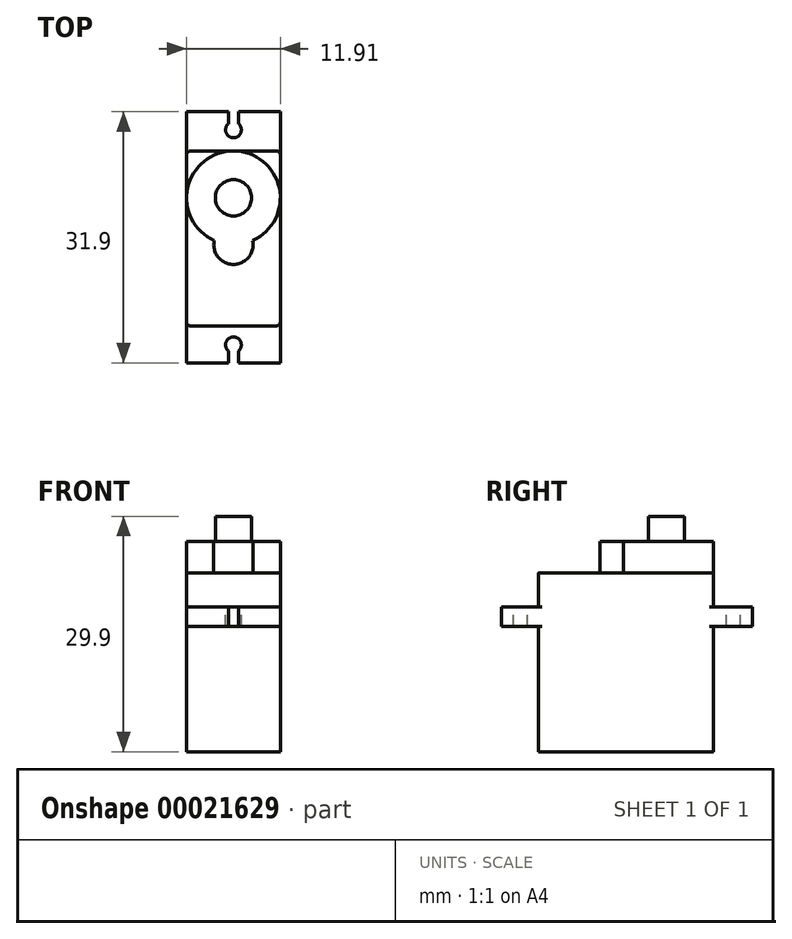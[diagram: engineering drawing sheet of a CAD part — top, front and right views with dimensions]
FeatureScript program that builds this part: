
annotation { "Feature Type Name" : "Feature", "Feature Type Description" : "" }
export const myFeature = defineFeature(function(context is Context, id is Id, definition is map)
    precondition{}
    {
        {
            var Q0;
            Q0=qCreatedBy(makeId("Top.planeOp"),FACE);
            var sketch = newSketch(context, id + "F0", { "sketchPlane" : qUnion([Q0])});
            skLineSegment(sketch, "E0", {"start": v(0, 0.5) * mm, "end": v(0, 21.73) * mm});
            skLineSegment(sketch, "E1", {"start": v(0.5, 22.23) * mm, "end": v(11.4, 22.23) * mm});
            skLineSegment(sketch, "E2", {"start": v(11.9, 21.73) * mm, "end": v(11.9, 0.5) * mm});
            skLineSegment(sketch, "E3", {"start": v(11.4, 0) * mm, "end": v(0.5, 0) * mm});
            skPoint(sketch, "E4.visualSharp", {"position": v(0, 22.23) * mm});
            skArc(sketch, "E4.filletArc", {"start": v(0.5, 22.23) * mm, "mid": v(0.15, 22.08) * mm, "end": v(0, 21.73) * mm});
            skPoint(sketch, "E5.visualSharp", {"position": v(11.9, 22.23) * mm});
            skArc(sketch, "E5.filletArc", {"start": v(11.9, 21.73) * mm, "mid": v(11.76, 22.08) * mm, "end": v(11.4, 22.23) * mm});
            skPoint(sketch, "E6.visualSharp", {"position": v(11.9, 0) * mm});
            skArc(sketch, "E6.filletArc", {"start": v(11.4, 0) * mm, "mid": v(11.76, 0.15) * mm, "end": v(11.9, 0.5) * mm});
            skPoint(sketch, "E7.visualSharp", {"position": v(0, 0) * mm});
            skArc(sketch, "E7.filletArc", {"start": v(0, 0.5) * mm, "mid": v(0.15, 0.15) * mm, "end": v(0.5, 0) * mm});
            skSolve(sketch);
        }
        {
            var Q0;
            Q0=makeQuery(id+"F0.imprint","IMPRINT",FACE,{"disambiguationData":[TD([[makeQuery(id+"F0.imprint","IMPRINT",EDGE,{"derivedFrom":sQuery(id+"F0.wireOp",EDGE,"E0")}),-1.0]])]});
            extrude(context, id + "F1", {"entities" : qUnion([Q0]), "depth" : 16 * mm});
        }
        {
            var Q0;
            Q0=makeQuery(id+"F1.opExtrude","CAP_FACE",FACE,{"disambiguationData":[OSD([sQuery(id+"F0.wireOp",EDGE,"E0"),sQuery(id+"F0.wireOp",EDGE,"E1"),sQuery(id+"F0.wireOp",EDGE,"E2"),sQuery(id+"F0.wireOp",EDGE,"E3"),sQuery(id+"F0.wireOp",EDGE,"E4.filletArc"),sQuery(id+"F0.wireOp",EDGE,"E5.filletArc"),sQuery(id+"F0.wireOp",EDGE,"E6.filletArc"),sQuery(id+"F0.wireOp",EDGE,"E7.filletArc")])],"isStart":false});
            extrude(context, id + "F2", {"entities" : qUnion([Q0]), "operationType" : NewBodyOperationType.ADD, "depth" : 6.7 * mm});
        }
        {
            var Q0;
            Q0=makeQuery(id+"F2.opExtrude","CAP_FACE",FACE,{"disambiguationData":[OSD([sQuery(id+"F0.wireOp",EDGE,"E0"),sQuery(id+"F0.wireOp",EDGE,"E1"),sQuery(id+"F0.wireOp",EDGE,"E2"),sQuery(id+"F0.wireOp",EDGE,"E3"),sQuery(id+"F0.wireOp",EDGE,"E4.filletArc"),sQuery(id+"F0.wireOp",EDGE,"E5.filletArc"),sQuery(id+"F0.wireOp",EDGE,"E6.filletArc"),sQuery(id+"F0.wireOp",EDGE,"E7.filletArc")])],"isStart":false});
            var sketch = newSketch(context, id + "F3", { "sketchPlane" : qUnion([Q0])});
            skLineSegment(sketch, "E8", {"start": v(0, 16.27) * mm, "end": v(11.9, 16.27) * mm, "construction": true});
            skArc(sketch, "E9", {"start": v(8.4, 10.84) * mm, "mid": v(5.95, 22.23) * mm, "end": v(3.5, 10.84) * mm});
            skLineSegment(sketch, "E10", {"start": v(5.95, 16.27) * mm, "end": v(5.95, 5.27) * mm, "construction": true});
            skArc(sketch, "E11", {"start": v(3.5, 10.84) * mm, "mid": v(5.95, 7.82) * mm, "end": v(8.4, 10.84) * mm});
            skSolve(sketch);
        }
        {
            var Q0;
            {var subQ0=sQuery(id+"F3.wireOp",EDGE,"E11");Q0=makeQuery(id+"F3.imprint","IMPRINT",FACE,{"disambiguationData":[TD([[makeQuery(id+"F3.imprint","IMPRINT",EDGE,{"derivedFrom":subQ0}),1.0]])]});}
            extrude(context, id + "F4", {"entities" : qUnion([Q0]), "operationType" : NewBodyOperationType.ADD, "depth" : 4 * mm});
        }
        {
            var Q0;
            Q0=makeQuery(id+"F4.opExtrude","CAP_FACE",FACE,{"disambiguationData":[OSD([sQuery(id+"F3.wireOp",EDGE,"E9"),sQuery(id+"F3.wireOp",EDGE,"E11")])],"isStart":false});
            var sketch = newSketch(context, id + "F5", { "sketchPlane" : qUnion([Q0])});
            skLineSegment(sketch, "E12", {"start": v(5.95, 22.23) * mm, "end": v(5.95, 7.82) * mm, "construction": true});
            skLineSegment(sketch, "E13", {"start": v(0, 16.27) * mm, "end": v(11.9, 16.27) * mm, "construction": true});
            skCircle(sketch, "E14", {"center": v(5.95, 16.27) * mm, "radius": 2.3 * mm});
            skSolve(sketch);
        }
        {
            var Q0;
            Q0=makeQuery(id+"F5.imprint","IMPRINT",FACE,{"disambiguationData":[TD([[makeQuery(id+"F5.imprint","IMPRINT",EDGE,{"derivedFrom":sQuery(id+"F5.wireOp",EDGE,"E14")}),1.0]])]});
            extrude(context, id + "F6", {"entities" : qUnion([Q0]), "operationType" : NewBodyOperationType.ADD, "depth" : 3.2 * mm});
        }
        {
            var Q0;
            {var subQ0=sQuery(id+"F0.wireOp",EDGE,"E3");Q0=makeQuery(id+"F2.boolean.opBoolean","MERGE",FACE,{"derivedFrom":[makeQuery(id+"F1.opExtrude","SWEPT_FACE",FACE,{"disambiguationData":[OSD([subQ0])]}),makeQuery(id+"F2.opExtrude","SWEPT_FACE",FACE,{"disambiguationData":[OSD([subQ0])]})]});}
            var sketch = newSketch(context, id + "F7", { "sketchPlane" : qUnion([Q0])});
            skLineSegment(sketch, "E15", {"start": v(5.95, 22.7) * mm, "end": v(5.95, 0) * mm, "construction": true});
            skLineSegment(sketch, "E16", {"start": v(0.5, 18.4) * mm, "end": v(11.4, 18.4) * mm, "construction": true});
            skLineSegment(sketch, "E17", {"start": v(0, 18.4) * mm, "end": v(11.9, 18.4) * mm});
            skLineSegment(sketch, "E18", {"start": v(11.9, 18.4) * mm, "end": v(11.9, 15.9) * mm});
            skLineSegment(sketch, "E19", {"start": v(11.9, 15.9) * mm, "end": v(0, 15.9) * mm});
            skLineSegment(sketch, "E20", {"start": v(0, 15.9) * mm, "end": v(0, 18.4) * mm});
            skSolve(sketch);
        }
        {
            var Q0;
            {var subQ7=sQuery(id+"F7.wireOp",EDGE,"E18");Q0=makeQuery(id+"F7.imprint","IMPRINT",FACE,{"disambiguationData":[TD([[makeQuery(id+"F7.imprint","IMPRINT",EDGE,{"derivedFrom":subQ7}),-1.0]])]});}
            var Q1;
            {var subQ0=sQuery(id+"F0.wireOp",EDGE,"E3");var subQ1=sQuery(id+"F0.wireOp",EDGE,"E7.filletArc");var subQ2=makeQuery(id+"F2.boolean.opBoolean","MERGE",EDGE,{"derivedFrom":[makeQuery(id+"F1.opExtrude","SWEPT_EDGE",EDGE,{"disambiguationData":[OSD([subQ0,subQ1])]}),makeQuery(id+"F2.opExtrude","SWEPT_EDGE",EDGE,{"disambiguationData":[OSD([subQ0,subQ1])]})]});var subQ5=sQuery(id+"F7.wireOp",EDGE,"E17");var subQ6=makeQuery(id+"F7.imprint","INTERSECT",VERTEX,{"derivedFrom":[subQ2,subQ5]});Q1=makeQuery(id+"F7.imprint","IMPRINT",FACE,{"disambiguationData":[TD([[makeQuery(id+"F7.imprint","IMPRINT",EDGE,{"disambiguationData":[TD([[subQ6,-1.0]])],"derivedFrom":subQ5}),-1.0]])]});}
            var Q2;
            {var subQ7=sQuery(id+"F7.wireOp",EDGE,"E20");Q2=makeQuery(id+"F7.imprint","IMPRINT",FACE,{"disambiguationData":[TD([[makeQuery(id+"F7.imprint","IMPRINT",EDGE,{"derivedFrom":subQ7}),-1.0]])]});}
            extrude(context, id + "F8", {"entities" : qUnion([Q0, Q1, Q2]), "operationType" : NewBodyOperationType.ADD, "oppositeDirection" : true, "depth" : 1 * mm});
        }
        {
            var Q0;
            {var subQ0=sQuery(id+"F0.wireOp",EDGE,"E3");Q0=makeQuery(id+"F8.boolean.opBoolean","MERGE",FACE,{"derivedFrom":[makeQuery(id+"F2.boolean.opBoolean","MERGE",FACE,{"derivedFrom":[makeQuery(id+"F1.opExtrude","SWEPT_FACE",FACE,{"disambiguationData":[OSD([subQ0])]}),makeQuery(id+"F2.opExtrude","SWEPT_FACE",FACE,{"disambiguationData":[OSD([subQ0])]})]}),makeQuery(id+"F8.opExtrude","CAP_FACE",FACE,{"disambiguationData":[OSD([sQuery(id+"F7.wireOp",EDGE,"E17"),sQuery(id+"F7.wireOp",EDGE,"E18"),sQuery(id+"F7.wireOp",EDGE,"E19"),sQuery(id+"F7.wireOp",EDGE,"E20")])],"isStart":true})]});}
            var sketch = newSketch(context, id + "F9", { "sketchPlane" : qUnion([Q0])});
            skLineSegment(sketch, "E21", {"start": v(0.5, 18.4) * mm, "end": v(11.4, 18.4) * mm});
            skLineSegment(sketch, "E22", {"start": v(0.5, 15.9) * mm, "end": v(11.4, 15.9) * mm});
            skSolve(sketch);
        }
        {
            var Q0;
            Q0=makeQuery(id+"F9.imprint","IMPRINT",FACE,{"disambiguationData":[TD([[makeQuery(id+"F9.imprint","IMPRINT",EDGE,{"derivedFrom":sQuery(id+"F9.wireOp",EDGE,"E21")}),-1.0]])]});
            extrude(context, id + "F10", {"entities" : qUnion([Q0]), "operationType" : NewBodyOperationType.ADD, "depth" : 4.7 * mm});
        }
        {
            var Q0;
            Q0=makeQuery(id+"F10.opExtrude","CAP_FACE",FACE,{"disambiguationData":[OSD([sQuery(id+"F7.wireOp",EDGE,"E17"),sQuery(id+"F7.wireOp",EDGE,"E18"),sQuery(id+"F7.wireOp",EDGE,"E19"),sQuery(id+"F7.wireOp",EDGE,"E20"),sQuery(id+"F9.wireOp",EDGE,"E21"),sQuery(id+"F9.wireOp",EDGE,"E22")])],"isStart":false});
            extrude(context, id + "F11", {"entities" : qUnion([Q0]), "operationType" : NewBodyOperationType.ADD, "oppositeDirection" : true, "depth" : 31.9 * mm});
        }
        {
            var Q0;
            {var subQ0=sQuery(id+"F7.wireOp",EDGE,"E17");var subQ1=makeQuery(id+"F8.opExtrude","SWEPT_FACE",FACE,{"disambiguationData":[OSD([subQ0])]});var subQ8=sQuery(id+"F0.wireOp",EDGE,"E0");var subQ10=sQuery(id+"F0.wireOp",EDGE,"E2");Q0=makeQuery(id+"F10.boolean.opBoolean","MERGE",FACE,{"derivedFrom":[makeQuery(id+"F8.boolean.opBoolean","SPLIT",FACE,{"disambiguationData":[TD([makeQuery(id+"F1.opExtrude","SWEPT_FACE",FACE,{"disambiguationData":[OSD([subQ8])]})])],"derivedFrom":subQ1}),makeQuery(id+"F8.boolean.opBoolean","SPLIT",FACE,{"disambiguationData":[TD([makeQuery(id+"F1.opExtrude","SWEPT_FACE",FACE,{"disambiguationData":[OSD([subQ10])]})])],"derivedFrom":subQ1}),makeQuery(id+"F10.opExtrude","SWEPT_FACE",FACE,{"disambiguationData":[OSD([subQ0,sQuery(id+"F9.wireOp",EDGE,"E21")])]})]});}
            var sketch = newSketch(context, id + "F12", { "sketchPlane" : qUnion([Q0])});
            skLineSegment(sketch, "E23", {"start": v(0, -2.4) * mm, "end": v(11.9, -2.4) * mm, "construction": true});
            skArc(sketch, "E24", {"start": v(6.6, -3.16) * mm, "mid": v(5.95, -1.4) * mm, "end": v(5.3, -3.16) * mm});
            skLineSegment(sketch, "E25", {"start": v(5.95, -2.4) * mm, "end": v(5.95, -4.7) * mm, "construction": true});
            skLineSegment(sketch, "E26", {"start": v(6.6, -4.7) * mm, "end": v(6.6, -3.16) * mm});
            skLineSegment(sketch, "E27", {"start": v(5.3, -4.7) * mm, "end": v(5.3, -3.16) * mm});
            skSolve(sketch);
        }
        {
            var Q0;
            Q0=makeQuery(id+"F12.imprint","IMPRINT",FACE,{"disambiguationData":[TD([[makeQuery(id+"F12.imprint","IMPRINT",EDGE,{"derivedFrom":sQuery(id+"F12.wireOp",EDGE,"E24")}),1.0]])]});
            extrude(context, id + "F13", {"entities" : qUnion([Q0]), "operationType" : NewBodyOperationType.REMOVE, "endBound" : BoundingType.UP_TO_NEXT, "oppositeDirection" : true, "depth" : 25.4 * mm});
        }
        {
            var Q0;
            Q0=makeQuery(id+"F11.opExtrude","SWEPT_FACE",FACE,{"disambiguationData":[OSD([sQuery(id+"F7.wireOp",EDGE,"E17"),sQuery(id+"F9.wireOp",EDGE,"E21")])]});
            var sketch = newSketch(context, id + "F14", { "sketchPlane" : qUnion([Q0])});
            skLineSegment(sketch, "E28", {"start": v(0, 24.9) * mm, "end": v(11.9, 24.9) * mm, "construction": true});
            skArc(sketch, "E29", {"start": v(5.3, 25.66) * mm, "mid": v(5.95, 23.9) * mm, "end": v(6.6, 25.66) * mm});
            skLineSegment(sketch, "E30", {"start": v(5.95, 24.9) * mm, "end": v(5.95, 27.2) * mm, "construction": true});
            skLineSegment(sketch, "E31", {"start": v(5.3, 27.2) * mm, "end": v(5.3, 25.66) * mm});
            skLineSegment(sketch, "E32", {"start": v(6.6, 27.2) * mm, "end": v(6.6, 25.66) * mm});
            skSolve(sketch);
        }
        {
            var Q0;
            Q0=makeQuery(id+"F14.imprint","IMPRINT",FACE,{"disambiguationData":[TD([[makeQuery(id+"F14.imprint","IMPRINT",EDGE,{"derivedFrom":sQuery(id+"F14.wireOp",EDGE,"E29")}),1.0]])]});
            extrude(context, id + "F15", {"entities" : qUnion([Q0]), "operationType" : NewBodyOperationType.REMOVE, "endBound" : BoundingType.UP_TO_NEXT, "oppositeDirection" : true, "depth" : 25.4 * mm});
        }
        {
            var Q0;
            Q0=makeQuery(id+"F1.opExtrude","SWEPT_BODY",BODY,{"disambiguationData":[OSD([sQuery(id+"F0.wireOp",EDGE,"E0"),sQuery(id+"F0.wireOp",EDGE,"E1"),sQuery(id+"F0.wireOp",EDGE,"E2"),sQuery(id+"F0.wireOp",EDGE,"E3"),sQuery(id+"F0.wireOp",EDGE,"E4.filletArc"),sQuery(id+"F0.wireOp",EDGE,"E5.filletArc"),sQuery(id+"F0.wireOp",EDGE,"E6.filletArc"),sQuery(id+"F0.wireOp",EDGE,"E7.filletArc")])]});
            transform(context, id + "F16", {"entities" : qUnion([Q0]), "transformType" : TransformType.TRANSLATION_3D, "dx" : 0 * mm, "dy" : 0 * mm, "dz" : 0 * mm, "makeCopy" : true});
        }
        {
            var Q0;
            Q0=makeQuery(id+"F16.opPattern","COPY",BODY,{"derivedFrom":makeQuery(id+"F1.opExtrude","SWEPT_BODY",BODY,{"disambiguationData":[OSD([sQuery(id+"F0.wireOp",EDGE,"E0"),sQuery(id+"F0.wireOp",EDGE,"E1"),sQuery(id+"F0.wireOp",EDGE,"E2"),sQuery(id+"F0.wireOp",EDGE,"E3"),sQuery(id+"F0.wireOp",EDGE,"E4.filletArc"),sQuery(id+"F0.wireOp",EDGE,"E5.filletArc"),sQuery(id+"F0.wireOp",EDGE,"E6.filletArc"),sQuery(id+"F0.wireOp",EDGE,"E7.filletArc")])]}),"instanceName":"1"});
            deleteBodies(context, id + "F17", {"entities" : qUnion([Q0])});
        }
    });
